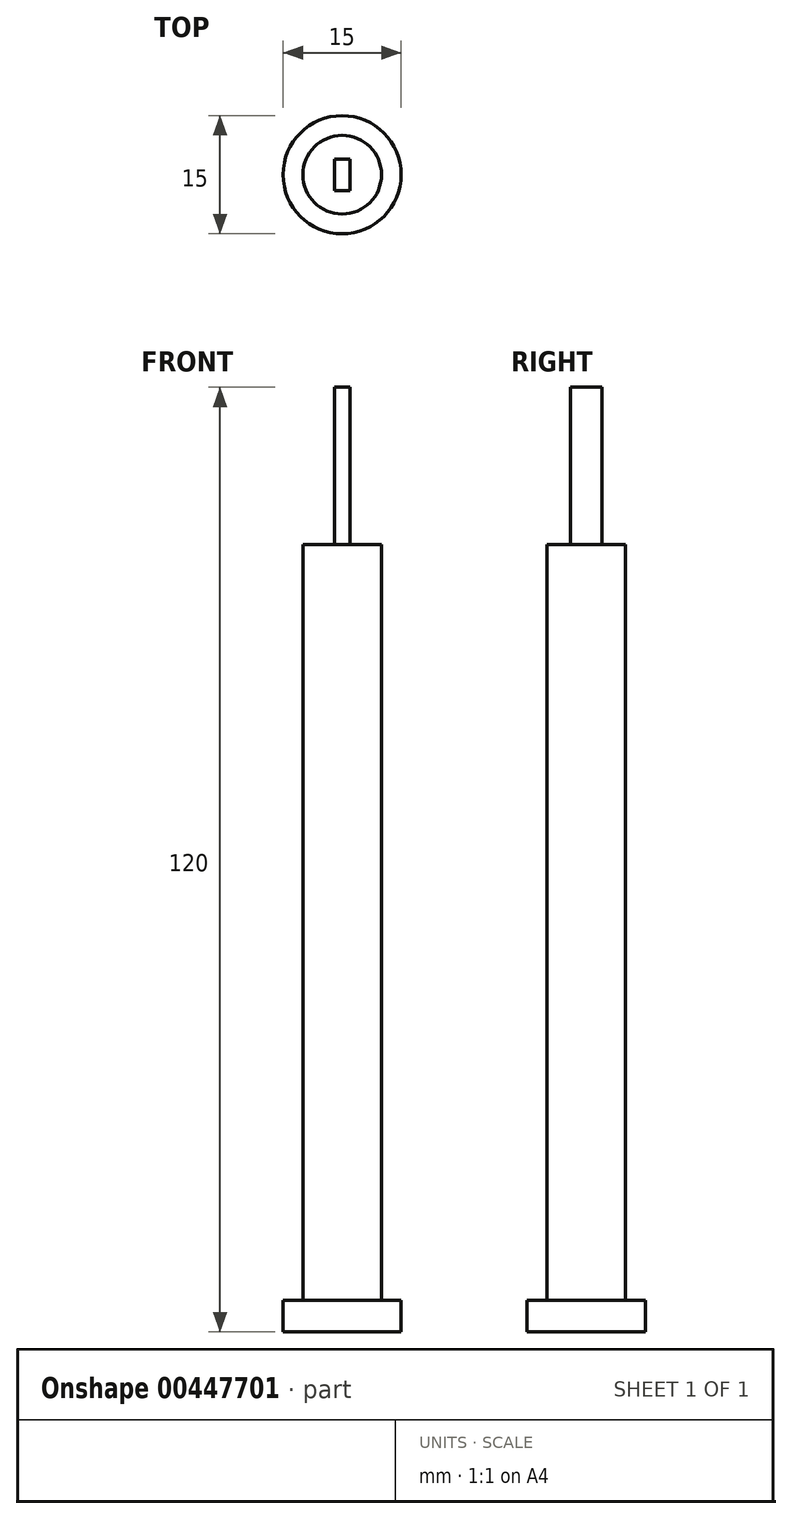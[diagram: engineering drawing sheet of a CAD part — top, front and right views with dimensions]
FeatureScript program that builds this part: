
annotation { "Feature Type Name" : "Feature", "Feature Type Description" : "" }
export const myFeature = defineFeature(function(context is Context, id is Id, definition is map)
    precondition{}
    {
        {
            var Q0;
            Q0=qCreatedBy(makeId("Top.planeOp"),FACE);
            var sketch = newSketch(context, id + "F0", { "sketchPlane" : qUnion([Q0])});
            skCircle(sketch, "E0", {"center": v(0, 0) * mm, "radius": 7.5 * mm});
            skSolve(sketch);
        }
        {
            var Q0;
            Q0=qSketchRegion(id+"F0",true);
            extrude(context, id + "F1", {"entities" : qUnion([Q0]), "depth" : 4 * mm});
        }
        {
            var Q0;
            Q0=qCreatedBy(makeId("Top.planeOp"),FACE);
            var sketch = newSketch(context, id + "F2", { "sketchPlane" : qUnion([Q0])});
            skCircle(sketch, "E1", {"center": v(0, 0) * mm, "radius": 5 * mm});
            skSolve(sketch);
        }
        {
            var Q0;
            Q0=qSketchRegion(id+"F2",true);
            extrude(context, id + "F3", {"entities" : qUnion([Q0]), "operationType" : NewBodyOperationType.ADD, "depth" : 100 * mm});
        }
        {
            var Q0;
            Q0=makeQuery(id+"F3.opExtrude","CAP_FACE",FACE,{"disambiguationData":[OSD([sQuery(id+"F2.wireOp",EDGE,"E1")])],"isStart":false});
            var sketch = newSketch(context, id + "F4", { "sketchPlane" : qUnion([Q0])});
            skLineSegment(sketch, "E2.bottom", {"start": v(-1, 2) * mm, "end": v(1, 2) * mm});
            skLineSegment(sketch, "E2.top", {"start": v(-1, -2) * mm, "end": v(1, -2) * mm});
            skLineSegment(sketch, "E2.left", {"start": v(-1, 2) * mm, "end": v(-1, -2) * mm});
            skLineSegment(sketch, "E2.right", {"start": v(1, 2) * mm, "end": v(1, -2) * mm});
            skSolve(sketch);
        }
        {
            var Q0;
            Q0=makeQuery(id+"F4.imprint","IMPRINT",FACE,{"disambiguationData":[TD([[makeQuery(id+"F4.imprint","IMPRINT",EDGE,{"derivedFrom":sQuery(id+"F4.wireOp",EDGE,"E2.bottom")}),-1.0]])]});
            extrude(context, id + "F5", {"entities" : qUnion([Q0]), "operationType" : NewBodyOperationType.ADD, "depth" : 20 * mm});
        }
    });
